# Revit family: FU_Modular_Sandler_Bau 5-3
name_source: partatom
category: Furniture
units: mm (PartAtom-declared; Revit-internal decimal feet)

## family parameters
Always vertical = Yes
Cut with Voids When Loaded = No
OmniClass Number = 23.21.23.00
Render Appearance Source = Family Geometry
Room Calculation Point = No
Shared = No
Work Plane-Based = No

## types (1)
- Bau 5.3
    Default Elevation = 0 mm  [stored 0 ft]
    Depth = 900 mm  [stored 2.95276 ft]
    Description = Open back easy chair with shell of fibre board and high resilient polyurethane foam. Adjustable glides.
    Height = 720 mm  [stored 2.3622 ft]
    Manufacturer = Sandler
    Model = Bau 5.3
    Product Material = Fabric - Manhattan - Staten YI386
    URL = https://www.sandlerseating.com
    Weight Net (Kg) = 21
    Width = 1010 mm  [stored 3.31365 ft]
    Z_Pouf = No

note: [stored X ft] marks values corroborated as IEEE doubles in the binary element streams (Revit-internal decimal feet)

## geometry (parser evidence)
native form markers: Sweep x2
no freeform markers — native parametric forms only
